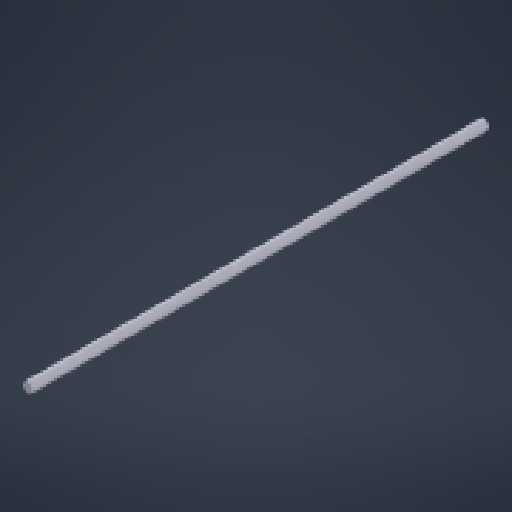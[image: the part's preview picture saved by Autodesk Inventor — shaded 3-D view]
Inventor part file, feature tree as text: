
AUTODESK INVENTOR PART (.ipt)
format: ipt  version: 2025.3 (Build 293356030, 356C)  size: 123,904 bytes
history: native  units: mm
features: extrude x2, sketch x2, other x1
ambient origin geometry x8: Origin, YZ Plane, XZ Plane, XY Plane, X Axis, Y Axis, Z Axis, Center Point
bodies: Body1 (feature_tree)
feature tree (5):
  other  "實體1"
  extrude  "擠出1"  Depth=5.0mm TaperAngle=0.0deg
  extrude  "擠出2"  Depth=5.0mm TaperAngle=0.0deg
  sketch  "草圖1"
  sketch  "草圖2"
